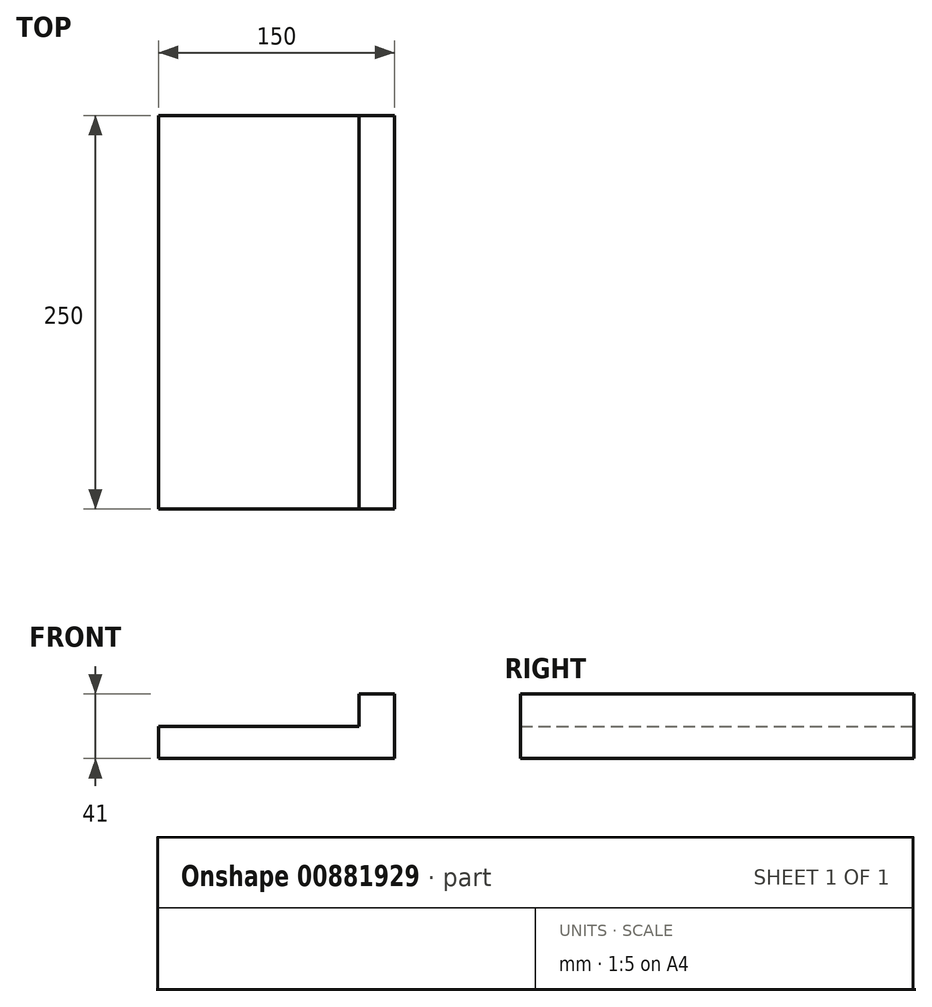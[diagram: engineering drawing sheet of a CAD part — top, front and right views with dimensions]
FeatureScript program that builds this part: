
annotation { "Feature Type Name" : "Feature", "Feature Type Description" : "" }
export const myFeature = defineFeature(function(context is Context, id is Id, definition is map)
    precondition{}
    {
        {
            var Q0;
            Q0=qCreatedBy(makeId("Front.planeOp"),FACE);
            var sketch = newSketch(context, id + "F0", { "sketchPlane" : qUnion([Q0])});
            skLineSegment(sketch, "E0.bottom", {"start": v(0, 0) * mm, "end": v(22.6, 0) * mm});
            skLineSegment(sketch, "E0.top", {"start": v(0, 20.5) * mm, "end": v(22.6, 20.5) * mm});
            skLineSegment(sketch, "E0.left", {"start": v(0, 0) * mm, "end": v(0, 20.5) * mm});
            skLineSegment(sketch, "E0.right", {"start": v(22.6, 0) * mm, "end": v(22.6, 20.5) * mm});
            skLineSegment(sketch, "E1.bottom", {"start": v(22.6, 0) * mm, "end": v(-127.4, 0) * mm});
            skLineSegment(sketch, "E1.top", {"start": v(22.6, -20.5) * mm, "end": v(-127.4, -20.5) * mm});
            skLineSegment(sketch, "E1.left", {"start": v(22.6, 0) * mm, "end": v(22.6, -20.5) * mm});
            skLineSegment(sketch, "E1.right", {"start": v(-127.4, 0) * mm, "end": v(-127.4, -20.5) * mm});
            skSolve(sketch);
        }
        {
            var Q0;
            Q0=makeQuery(id+"F0.imprint","IMPRINT",FACE,{"disambiguationData":[TD([[makeQuery(id+"F0.imprint","IMPRINT",EDGE,{"derivedFrom":sQuery(id+"F0.wireOp",EDGE,"E1.top")}),-1.0]])]});
            var Q1;
            Q1=makeQuery(id+"F0.imprint","IMPRINT",FACE,{"disambiguationData":[TD([[makeQuery(id+"F0.imprint","IMPRINT",EDGE,{"derivedFrom":sQuery(id+"F0.wireOp",EDGE,"E0.top")}),-1.0]])]});
            extrude(context, id + "F1", {"entities" : qUnion([Q0, Q1]), "depth" : 250 * mm, "offsetDistance" : 25 * mm});
        }
    });
